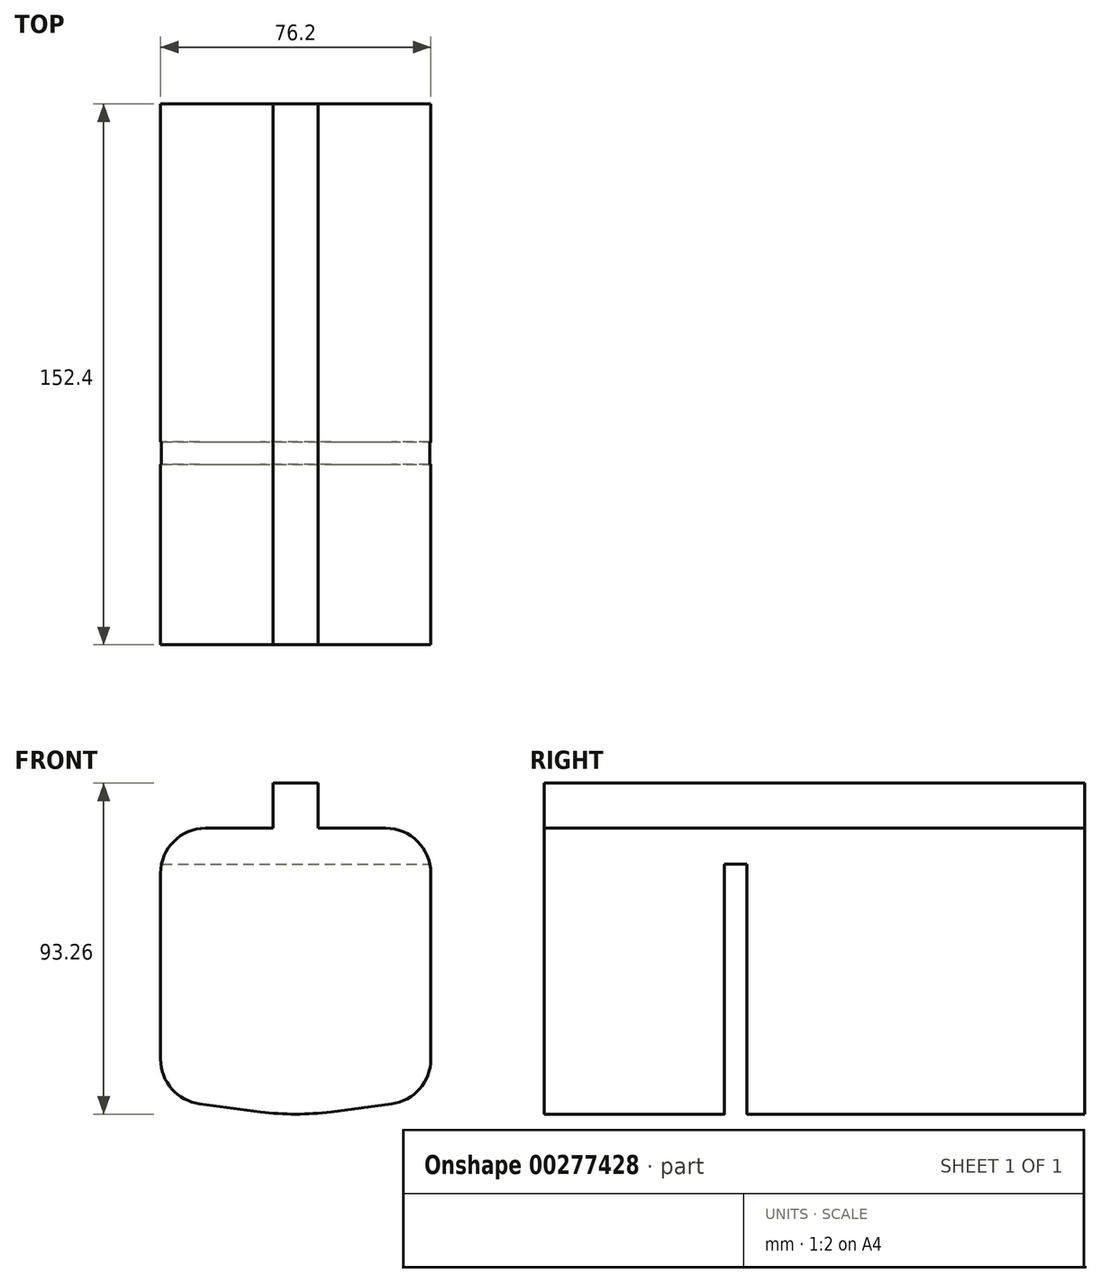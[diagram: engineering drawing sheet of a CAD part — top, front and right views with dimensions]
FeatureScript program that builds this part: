
annotation { "Feature Type Name" : "Feature", "Feature Type Description" : "" }
export const myFeature = defineFeature(function(context is Context, id is Id, definition is map)
    precondition{}
    {
        {
            var Q0;
            Q0=qCreatedBy(makeId("Front.planeOp"),FACE);
            var sketch = newSketch(context, id + "F0", { "sketchPlane" : qUnion([Q0])});
            skLineSegment(sketch, "E0", {"start": v(-6.35, 81.22) * mm, "end": v(-6.35, 93.92) * mm});
            skLineSegment(sketch, "E1", {"start": v(-6.35, 93.92) * mm, "end": v(6.35, 93.92) * mm});
            skLineSegment(sketch, "E2", {"start": v(6.35, 93.92) * mm, "end": v(6.35, 81.22) * mm});
            skLineSegment(sketch, "E3", {"start": v(6.35, 81.22) * mm, "end": v(38.1, 81.22) * mm});
            skLineSegment(sketch, "E4", {"start": v(38.1, 81.22) * mm, "end": v(38.1, 5.02) * mm});
            skLineSegment(sketch, "E5", {"start": v(38.1, 5.02) * mm, "end": v(9.95, 1.3) * mm});
            skLineSegment(sketch, "E6", {"start": v(-9.95, 1.3) * mm, "end": v(-38.1, 5.02) * mm});
            skLineSegment(sketch, "E7", {"start": v(-38.1, 5.02) * mm, "end": v(-38.1, 81.22) * mm});
            skLineSegment(sketch, "E8", {"start": v(-38.1, 81.22) * mm, "end": v(-6.35, 81.22) * mm});
            skPoint(sketch, "E9.visualSharp", {"position": v(0, 0) * mm});
            skArc(sketch, "E9.filletArc", {"start": v(-9.95, 1.3) * mm, "mid": v(0, 0.66) * mm, "end": v(9.95, 1.3) * mm});
            skPoint(sketch, "E10", {"position": v(0, 93.92) * mm});
            skSolve(sketch);
        }
        {
            var Q0;
            Q0 = qSketchRegion(id + "F0", true);
            extrude(context, id + "F1", {"entities" : qUnion([Q0]), "depth" : 152.4 * mm});
        }
        {
            var Q0;
            Q0=makeQuery(id+"F1.opExtrude","SWEPT_EDGE",EDGE,{"disambiguationData":[OSD([sQuery(id+"F0.wireOp",EDGE,"E3"),sQuery(id+"F0.wireOp",EDGE,"E4")])]});
            var Q1;
            Q1=makeQuery(id+"F1.opExtrude","SWEPT_EDGE",EDGE,{"disambiguationData":[OSD([sQuery(id+"F0.wireOp",EDGE,"E7"),sQuery(id+"F0.wireOp",EDGE,"E8")])]});
            var Q2;
            Q2=makeQuery(id+"F1.opExtrude","SWEPT_EDGE",EDGE,{"disambiguationData":[OSD([sQuery(id+"F0.wireOp",EDGE,"E6"),sQuery(id+"F0.wireOp",EDGE,"E7")])]});
            var Q3;
            Q3=makeQuery(id+"F1.opExtrude","SWEPT_EDGE",EDGE,{"disambiguationData":[OSD([sQuery(id+"F0.wireOp",EDGE,"E4"),sQuery(id+"F0.wireOp",EDGE,"E5")])]});
            fillet(context, id + "F2", {"entities" : qUnion([Q0, Q1, Q2, Q3]), "radius" : 12.7 * mm, "tangentPropagation" : true, "allowEdgeOverflow" : false});
        }
        {
            var Q0;
            Q0=qCreatedBy(makeId("Right.planeOp"),FACE);
            var sketch = newSketch(context, id + "F3", { "sketchPlane" : qUnion([Q0])});
            skLineSegment(sketch, "E11.bottom", {"start": v(-101.6, -5.04) * mm, "end": v(-95.25, -5.04) * mm});
            skLineSegment(sketch, "E11.top", {"start": v(-101.6, 71.16) * mm, "end": v(-95.25, 71.16) * mm});
            skLineSegment(sketch, "E11.left", {"start": v(-101.6, -5.04) * mm, "end": v(-101.6, 71.16) * mm});
            skLineSegment(sketch, "E11.right", {"start": v(-95.25, -5.04) * mm, "end": v(-95.25, 71.16) * mm});
            skPoint(sketch, "E12", {"position": v(-98.43, -5.04) * mm});
            skSolve(sketch);
        }
        {
            var Q0;
            Q0 = qSketchRegion(id + "F3", true);
            extrude(context, id + "F4", {"entities" : qUnion([Q0]), "operationType" : NewBodyOperationType.REMOVE, "endBound" : BoundingType.THROUGH_ALL, "oppositeDirection" : true, "depth" : 25.4 * mm, "hasSecondDirection" : true, "secondDirectionBound" : SecondDirectionBoundingType.THROUGH_ALL, "secondDirectionOppositeDirection" : false, "secondDirectionDepth" : 25.4 * mm});
        }
    });
